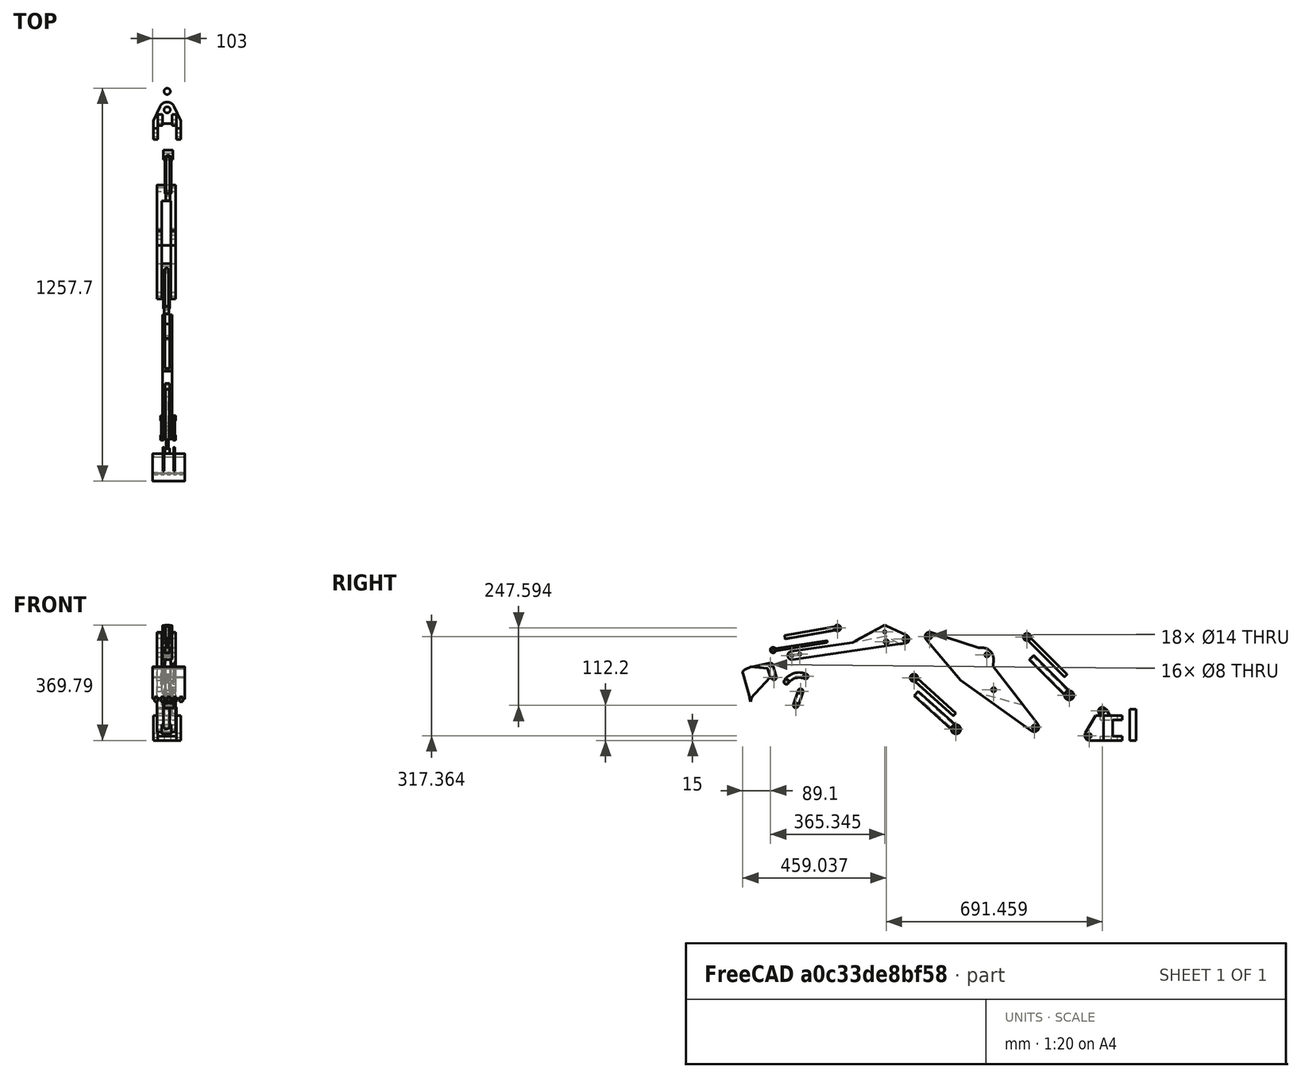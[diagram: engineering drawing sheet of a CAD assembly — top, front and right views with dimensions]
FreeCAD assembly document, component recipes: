
FREECAD ASSEMBLY — COMPONENT RECIPES ("AssemblyExample")

This assembly document has 13 components, labeled P0..P12 below (a component is one placed body or linked part). 0 of them carry a construction recipe — the FreeCAD feature program that regenerates the part from scratch, quoted from this document or its linked companion documents; the rest are supplied as boundary geometry only. No exploded tour is included for this assembly.
COMPONENT P0 — geometry summary ("Base001"; no construction recipe available for this part):
  bounding box: 119.7 x 106.0 x 88.3 mm
  tessellated surface: 4,364 triangles
  volume: 241281 mm^3 (22% of its bounding box)
  symmetry: mirror-symmetric across its x mid-plane
COMPONENT P1 — geometry summary ("BasePin001"; no construction recipe available for this part):
  bounding box: 100.0 x 20.0 x 20.0 mm
  tessellated surface: 500 triangles
  volume: 31416 mm^3 (79% of its bounding box)
  symmetry: 2-fold rotationally symmetric about the x axis; revolution-symmetric about the z axis through its bounding-box center; mirror-symmetric across its x mid-plane, y mid-plane, z mid-plane
COMPONENT P2 — geometry summary ("Boom001"; no construction recipe available for this part):
  bounding box: 436.3 x 203.7 x 60.9 mm
  tessellated surface: 4,520 triangles
  volume: 1204575 mm^3 (22% of its bounding box)
  symmetry: mirror-symmetric across its x mid-plane
COMPONENT P3 — geometry summary ("BoomCylinderInner001"; no construction recipe available for this part):
  bounding box: 177.3 x 82.0 x 15.1 mm
  tessellated surface: 1,472 triangles
  volume: 22989 mm^3 (10% of its bounding box)
COMPONENT P4 — geometry summary ("BoomCylinderOuter001"; no construction recipe available for this part):
  bounding box: 177.7 x 87.1 x 30.1 mm
  tessellated surface: 1,966 triangles
  volume: 48197 mm^3 (10% of its bounding box)
  symmetry: mirror-symmetric across its x mid-plane
COMPONENT P5 — geometry summary ("Bucket001"; no construction recipe available for this part):
  bounding box: 117.6 x 103.4 x 100.6 mm
  tessellated surface: 3,994 triangles
  volume: 58312 mm^3 (5% of its bounding box)
  symmetry: mirror-symmetric across its x mid-plane
COMPONENT P6 — geometry summary ("BucketCylinderInner001"; no construction recipe available for this part):
  bounding box: 173.2 x 77.1 x 15.1 mm
  tessellated surface: 1,172 triangles
  volume: 9046 mm^3 (4% of its bounding box)
COMPONENT P7 — geometry summary ("BucketCylinderOuter001"; no construction recipe available for this part):
  bounding box: 171.1 x 78.8 x 15.1 mm
  tessellated surface: 1,556 triangles
  volume: 16012 mm^3 (8% of its bounding box)
COMPONENT P8 — geometry summary ("BucketLink004"; no construction recipe available for this part):
  bounding box: 62.9 x 30.3 x 26.8 mm
  tessellated surface: 3,660 triangles
  volume: 12304 mm^3 (24% of its bounding box)
  symmetry: mirror-symmetric across its x mid-plane
COMPONENT P9 — geometry summary ("BucketLink003"; no construction recipe available for this part):
  bounding box: 73.0 x 48.2 x 47.1 mm
  tessellated surface: 4,141 triangles
  volume: 17079 mm^3 (10% of its bounding box)
COMPONENT P10 — geometry summary ("Stick001"; no construction recipe available for this part):
  bounding box: 379.8 x 121.2 x 31.8 mm
  tessellated surface: 3,756 triangles
  volume: 333942 mm^3 (23% of its bounding box)
COMPONENT P11 — geometry summary ("StickCylinderInner001"; no construction recipe available for this part):
  bounding box: 184.3 x 56.4 x 15.1 mm
  tessellated surface: 1,472 triangles
  volume: 22989 mm^3 (15% of its bounding box)
COMPONENT P12 — geometry summary ("StickCylinderOuter001"; no construction recipe available for this part):
  bounding box: 184.0 x 62.4 x 30.1 mm
  tessellated surface: 1,966 triangles
  volume: 48197 mm^3 (14% of its bounding box)
  symmetry: mirror-symmetric across its x mid-plane
PROVENANCE & LICENSES
A FreeCAD (.FCStd) document from a public repository crawl; recipes are the document's own serialized feature recipes (and, for linked parts, companion documents' recipes).
License: as declared in the source repository (recorded in the dataset sidecar).
